# Revit family: WLV_A3-Louvre-Blade
name_source: partatom
category: Specialty Equipment
revit_build: Autodesk Revit 2016 (Build: 20150220_1215(x64)
units: mm (PartAtom-declared; Revit-internal decimal feet)

## family parameters
Always vertical = Yes
Cut with Voids When Loaded = No
Part Type = Normal
Room Calculation Point = No
Round Connector Dimension = Use Diameter
Shared = No
Work Plane-Based = No

## types (7) — shared parameters

## per-type parameters (varying)
| type | Blade height |
| Louvre Blade | 2781 mm  [stored 9.12402 ft] |
| Louvre Blade 6 | 3125 mm  [stored 10.2526 ft] |
| Louvre Blade 5 | 2850 mm  [stored 9.35039 ft] |
| Louvre Blade 4 | 2225 mm |
| Louvre Blade 3 | 2850 mm  [stored 9.35039 ft] |
| Louvre Blade 2 | 3400 mm  [stored 11.1549 ft] |
| Louvre Blade 1 | 2850 mm  [stored 9.35039 ft] |

note: [stored X ft] marks values corroborated as IEEE doubles in the binary element streams (Revit-internal decimal feet)

## geometry (parser evidence)
native form markers: Sweep x3
no freeform markers — native parametric forms only
